# Revit family: BIMLIB_ПриточнаяУстановка_Eco-Slim1100-W_SHUFT
name_source: partatom
category: Оборудование
revit_build: Autodesk Revit 2017 (Build: 20170118_1100(x64)
units: mm (PartAtom-declared; Revit-internal decimal feet)

## family parameters
Всегда вертикально = Да
На основе рабочей плоскости = Нет
Общий = Нет
При загрузке вырезать с полостями = Нет
Размер круглого соединителя = Использовать диаметр
Тип детали = Нормальный
Точка расчета площади = Нет

## types (1)
- Eco-Slim 1100-W 17,0 кВт
    ADSK_URL документации изделия = http://www.shuft.ru
    ADSK_URL страницы изделия = http://www.shuft.ru
    ADSK_Версия Revit = 2017
    ADSK_Версия семейства = v.1
    ADSK_Единица измерения = шт.
    ADSK_Завод-изготовитель = ООО «Завод ВКО» марка SHUFT
    ADSK_Классификация нагрузок = Прочее
    ADSK_Код изделия = Eco-Slim 1100-W 17,0 кВт
    ADSK_Количество фаз = 1
    ADSK_Коэффициент мощности = 1
    ADSK_Марка = Eco-Slim 1100-W 17,0 кВт
    ADSK_Масса = 74
    ADSK_Масса_Текст = 74
    ADSK_Материал = BIMLIB_Сталь_SHUFT
    ADSK_Наименование = Приточная вентиляционная установка Eco-Slim 1100-W 17,0 кВт
    ADSK_Напряжение = 230 В
    ADSK_Номинальная мощность = 17000 Вт
    ADSK_Полная мощность = 17000 В·А
    ADSK_Размер_Высота = 255 мм
    ADSK_Размер_Длина = 1370 мм
    ADSK_Размер_Ширина = 760 мм
    ADSK_Тип воздушного фильтра = G4
    ADSK_Ток = 1 А
    ADSK_Частота вращения вентилятора = 2250
    BL_BIM library = https://bimlib.pro
    D = 160 мм
    H1 = 250 мм
    L2 = 1300 мм
    SH_Мощность вентилятора = 290 Вт
    URL = http://www.shuft.ru
    W3 = 500 мм
    Высота коннекторов = 128 мм
    Диаметр_патрубков = 20 мм
    Изготовитель = ООО «Завод ВКО» марка SHUFT
    Описание = Приточная установка ECO-SLIM выпускается в двух модификациях: или с водным нагреваем (модель 1100) или с электрическим нагревателем. В обеих модификациях воздушный клапан размещен снаружи корпуса, что улучшает его ремонтопригодность и позволяет выносить клапан с приводом к месту забора наружного воздуха. Установка обладает компактными габаритами и низким уровнем шума, что значительно упрощает выбор его размещения в квартире
